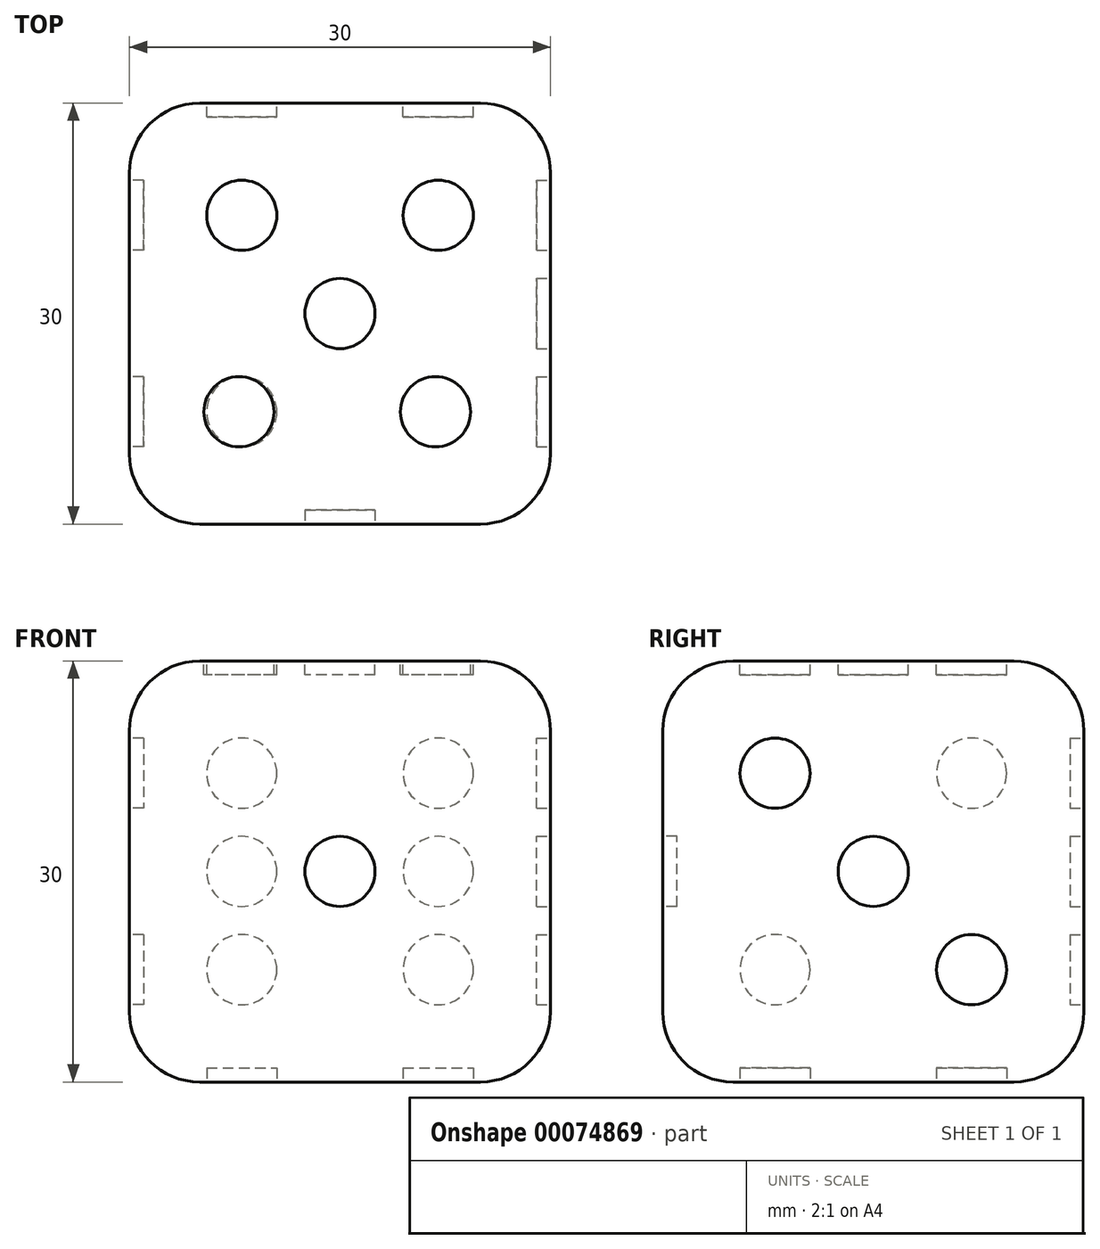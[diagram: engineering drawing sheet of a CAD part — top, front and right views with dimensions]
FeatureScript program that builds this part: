
annotation { "Feature Type Name" : "Feature", "Feature Type Description" : "" }
export const myFeature = defineFeature(function(context is Context, id is Id, definition is map)
    precondition{}
    {
        {
            var Q0;
            Q0=qCreatedBy(makeId("Front.planeOp"),FACE);
            var sketch = newSketch(context, id + "F0", { "sketchPlane" : qUnion([Q0])});
            skLineSegment(sketch, "E0.rect.bottom", {"start": v(-15, 15) * mm, "end": v(15, 15) * mm});
            skLineSegment(sketch, "E0.rect.top", {"start": v(-15, -15) * mm, "end": v(15, -15) * mm});
            skLineSegment(sketch, "E0.rect.left", {"start": v(-15, 15) * mm, "end": v(-15, -15) * mm});
            skLineSegment(sketch, "E0.rect.right", {"start": v(15, 15) * mm, "end": v(15, -15) * mm});
            skPoint(sketch, "E0.rect.middle", {"position": v(0, 0) * mm});
            skSolve(sketch);
        }
        {
            var Q0;
            Q0=makeQuery(id+"F0.imprint","IMPRINT",FACE,{"disambiguationData":[TD([[makeQuery(id+"F0.imprint","IMPRINT",EDGE,{"derivedFrom":sQuery(id+"F0.wireOp",EDGE,"E0.rect.bottom")}),-1.0]])]});
            extrude(context, id + "F1", {"entities" : qUnion([Q0]), "endBound" : BoundingType.SYMMETRIC, "depth" : 30 * mm});
        }
        {
            var Q0;
            Q0=makeQuery(id+"F1.opExtrude","CAP_FACE",FACE,{"disambiguationData":[OSD([sQuery(id+"F0.wireOp",EDGE,"E0.rect.bottom"),sQuery(id+"F0.wireOp",EDGE,"E0.rect.top"),sQuery(id+"F0.wireOp",EDGE,"E0.rect.left"),sQuery(id+"F0.wireOp",EDGE,"E0.rect.right")])],"isStart":false});
            var sketch = newSketch(context, id + "F2", { "sketchPlane" : qUnion([Q0])});
            skCircle(sketch, "E1", {"center": v(0, 0) * mm, "radius": 2.5 * mm});
            skSolve(sketch);
        }
        {
            var Q0;
            Q0=makeQuery(id+"F2.imprint","IMPRINT",FACE,{"disambiguationData":[TD([[makeQuery(id+"F2.imprint","IMPRINT",EDGE,{"derivedFrom":sQuery(id+"F2.wireOp",EDGE,"E1")}),1.0]])]});
            extrude(context, id + "F3", {"entities" : qUnion([Q0]), "operationType" : NewBodyOperationType.REMOVE, "oppositeDirection" : true, "depth" : 1 * mm});
        }
        {
            var Q0;
            Q0=makeQuery(id+"F1.opExtrude","CAP_FACE",FACE,{"disambiguationData":[OSD([sQuery(id+"F0.wireOp",EDGE,"E0.rect.bottom"),sQuery(id+"F0.wireOp",EDGE,"E0.rect.top"),sQuery(id+"F0.wireOp",EDGE,"E0.rect.left"),sQuery(id+"F0.wireOp",EDGE,"E0.rect.right")])],"isStart":true});
            var sketch = newSketch(context, id + "F4", { "sketchPlane" : qUnion([Q0])});
            skCircle(sketch, "E2", {"center": v(-7, 7) * mm, "radius": 2.5 * mm});
            skCircle(sketch, "E3.0.1.0", {"center": v(-7, 0) * mm, "radius": 2.5 * mm});
            skCircle(sketch, "E3.0.2.0", {"center": v(-7, -7) * mm, "radius": 2.5 * mm});
            skCircle(sketch, "E3.1.0.0", {"center": v(7, 7) * mm, "radius": 2.5 * mm});
            skCircle(sketch, "E3.1.1.0", {"center": v(7, 0) * mm, "radius": 2.5 * mm});
            skCircle(sketch, "E3.1.2.0", {"center": v(7, -7) * mm, "radius": 2.5 * mm});
            skLineSegment(sketch, "E3.direction1", {"start": v(-7, 7) * mm, "end": v(7, 7) * mm, "construction": true});
            skLineSegment(sketch, "E3.direction2", {"start": v(-7, 7) * mm, "end": v(-7, 0) * mm, "construction": true});
            skSolve(sketch);
        }
        {
            var Q0;
            Q0=makeQuery(id+"F4.imprint","IMPRINT",FACE,{"disambiguationData":[TD([[makeQuery(id+"F4.imprint","IMPRINT",EDGE,{"derivedFrom":sQuery(id+"F4.wireOp",EDGE,"E2")}),1.0]])]});
            var Q1;
            Q1=makeQuery(id+"F4.imprint","IMPRINT",FACE,{"disambiguationData":[TD([[makeQuery(id+"F4.imprint","IMPRINT",EDGE,{"derivedFrom":sQuery(id+"F4.wireOp",EDGE,"E3.0.1.0")}),1.0]])]});
            var Q2;
            Q2=makeQuery(id+"F4.imprint","IMPRINT",FACE,{"disambiguationData":[TD([[makeQuery(id+"F4.imprint","IMPRINT",EDGE,{"derivedFrom":sQuery(id+"F4.wireOp",EDGE,"E3.0.2.0")}),1.0]])]});
            var Q3;
            Q3=makeQuery(id+"F4.imprint","IMPRINT",FACE,{"disambiguationData":[TD([[makeQuery(id+"F4.imprint","IMPRINT",EDGE,{"derivedFrom":sQuery(id+"F4.wireOp",EDGE,"E3.1.2.0")}),1.0]])]});
            var Q4;
            Q4=makeQuery(id+"F4.imprint","IMPRINT",FACE,{"disambiguationData":[TD([[makeQuery(id+"F4.imprint","IMPRINT",EDGE,{"derivedFrom":sQuery(id+"F4.wireOp",EDGE,"E3.1.1.0")}),1.0]])]});
            var Q5;
            Q5=makeQuery(id+"F4.imprint","IMPRINT",FACE,{"disambiguationData":[TD([[makeQuery(id+"F4.imprint","IMPRINT",EDGE,{"derivedFrom":sQuery(id+"F4.wireOp",EDGE,"E3.1.0.0")}),1.0]])]});
            extrude(context, id + "F5", {"entities" : qUnion([Q0, Q1, Q2, Q3, Q4, Q5]), "operationType" : NewBodyOperationType.REMOVE, "oppositeDirection" : true, "depth" : 1 * mm});
        }
        {
            var Q0;
            Q0=makeQuery(id+"F1.opExtrude","SWEPT_FACE",FACE,{"disambiguationData":[OSD([sQuery(id+"F0.wireOp",EDGE,"E0.rect.right")])]});
            var sketch = newSketch(context, id + "F6", { "sketchPlane" : qUnion([Q0])});
            skCircle(sketch, "E4", {"center": v(0, 0) * mm, "radius": 2.5 * mm});
            skCircle(sketch, "E5", {"center": v(-7, 7) * mm, "radius": 2.5 * mm});
            skCircle(sketch, "E6", {"center": v(7, -7) * mm, "radius": 2.5 * mm});
            skSolve(sketch);
        }
        {
            var Q0;
            Q0=makeQuery(id+"F6.imprint","IMPRINT",FACE,{"disambiguationData":[TD([[makeQuery(id+"F6.imprint","IMPRINT",EDGE,{"derivedFrom":sQuery(id+"F6.wireOp",EDGE,"E5")}),1.0]])]});
            var Q1;
            Q1=makeQuery(id+"F6.imprint","IMPRINT",FACE,{"disambiguationData":[TD([[makeQuery(id+"F6.imprint","IMPRINT",EDGE,{"derivedFrom":sQuery(id+"F6.wireOp",EDGE,"E4")}),1.0]])]});
            var Q2;
            Q2=makeQuery(id+"F6.imprint","IMPRINT",FACE,{"disambiguationData":[TD([[makeQuery(id+"F6.imprint","IMPRINT",EDGE,{"derivedFrom":sQuery(id+"F6.wireOp",EDGE,"E6")}),1.0]])]});
            extrude(context, id + "F7", {"entities" : qUnion([Q0, Q1, Q2]), "operationType" : NewBodyOperationType.REMOVE, "oppositeDirection" : true, "depth" : 1 * mm});
        }
        {
            var Q0;
            Q0=makeQuery(id+"F1.opExtrude","SWEPT_FACE",FACE,{"disambiguationData":[OSD([sQuery(id+"F0.wireOp",EDGE,"E0.rect.left")])]});
            var sketch = newSketch(context, id + "F8", { "sketchPlane" : qUnion([Q0])});
            skCircle(sketch, "E7", {"center": v(-7, 7) * mm, "radius": 2.5 * mm});
            skCircle(sketch, "E8.0.1.0", {"center": v(-7, -7) * mm, "radius": 2.5 * mm});
            skCircle(sketch, "E8.1.0.0", {"center": v(7, 7) * mm, "radius": 2.5 * mm});
            skCircle(sketch, "E8.1.1.0", {"center": v(7, -7) * mm, "radius": 2.5 * mm});
            skLineSegment(sketch, "E8.direction1", {"start": v(-7, 7) * mm, "end": v(7, 7) * mm, "construction": true});
            skLineSegment(sketch, "E8.direction2", {"start": v(-7, 7) * mm, "end": v(-7, -7) * mm, "construction": true});
            skSolve(sketch);
        }
        {
            var Q0;
            Q0=makeQuery(id+"F8.imprint","IMPRINT",FACE,{"disambiguationData":[TD([[makeQuery(id+"F8.imprint","IMPRINT",EDGE,{"derivedFrom":sQuery(id+"F8.wireOp",EDGE,"E7")}),1.0]])]});
            var Q1;
            Q1=makeQuery(id+"F8.imprint","IMPRINT",FACE,{"disambiguationData":[TD([[makeQuery(id+"F8.imprint","IMPRINT",EDGE,{"derivedFrom":sQuery(id+"F8.wireOp",EDGE,"E8.1.0.0")}),1.0]])]});
            var Q2;
            Q2=makeQuery(id+"F8.imprint","IMPRINT",FACE,{"disambiguationData":[TD([[makeQuery(id+"F8.imprint","IMPRINT",EDGE,{"derivedFrom":sQuery(id+"F8.wireOp",EDGE,"E8.1.1.0")}),1.0]])]});
            var Q3;
            Q3=makeQuery(id+"F8.imprint","IMPRINT",FACE,{"disambiguationData":[TD([[makeQuery(id+"F8.imprint","IMPRINT",EDGE,{"derivedFrom":sQuery(id+"F8.wireOp",EDGE,"E8.0.1.0")}),1.0]])]});
            extrude(context, id + "F9", {"entities" : qUnion([Q0, Q1, Q2, Q3]), "operationType" : NewBodyOperationType.REMOVE, "oppositeDirection" : true, "depth" : 1 * mm});
        }
        {
            var Q0;
            Q0=makeQuery(id+"F1.opExtrude","SWEPT_FACE",FACE,{"disambiguationData":[OSD([sQuery(id+"F0.wireOp",EDGE,"E0.rect.bottom")])]});
            var sketch = newSketch(context, id + "F10", { "sketchPlane" : qUnion([Q0])});
            skCircle(sketch, "E9", {"center": v(0, 0) * mm, "radius": 2.5 * mm});
            skCircle(sketch, "E10", {"center": v(-7, 7) * mm, "radius": 2.5 * mm});
            skCircle(sketch, "E11.0.1.0", {"center": v(-7.2, -7) * mm, "radius": 2.5 * mm});
            skCircle(sketch, "E11.1.0.0", {"center": v(7, 7) * mm, "radius": 2.5 * mm});
            skCircle(sketch, "E11.1.1.0", {"center": v(6.8, -7) * mm, "radius": 2.5 * mm});
            skLineSegment(sketch, "E11.direction1", {"start": v(-7, 7) * mm, "end": v(7, 7) * mm, "construction": true});
            skLineSegment(sketch, "E11.direction2", {"start": v(-7, 7) * mm, "end": v(-7.2, -7) * mm, "construction": true});
            skSolve(sketch);
        }
        {
            var Q0;
            Q0=makeQuery(id+"F10.imprint","IMPRINT",FACE,{"disambiguationData":[TD([[makeQuery(id+"F10.imprint","IMPRINT",EDGE,{"derivedFrom":sQuery(id+"F10.wireOp",EDGE,"E11.1.1.0")}),1.0]])]});
            var Q1;
            Q1=makeQuery(id+"F10.imprint","IMPRINT",FACE,{"disambiguationData":[TD([[makeQuery(id+"F10.imprint","IMPRINT",EDGE,{"derivedFrom":sQuery(id+"F10.wireOp",EDGE,"E11.0.1.0")}),1.0]])]});
            var Q2;
            Q2=makeQuery(id+"F10.imprint","IMPRINT",FACE,{"disambiguationData":[TD([[makeQuery(id+"F10.imprint","IMPRINT",EDGE,{"derivedFrom":sQuery(id+"F10.wireOp",EDGE,"E9")}),1.0]])]});
            var Q3;
            Q3=makeQuery(id+"F10.imprint","IMPRINT",FACE,{"disambiguationData":[TD([[makeQuery(id+"F10.imprint","IMPRINT",EDGE,{"derivedFrom":sQuery(id+"F10.wireOp",EDGE,"E11.1.0.0")}),1.0]])]});
            var Q4;
            Q4=makeQuery(id+"F10.imprint","IMPRINT",FACE,{"disambiguationData":[TD([[makeQuery(id+"F10.imprint","IMPRINT",EDGE,{"derivedFrom":sQuery(id+"F10.wireOp",EDGE,"E10")}),1.0]])]});
            extrude(context, id + "F11", {"entities" : qUnion([Q0, Q1, Q2, Q3, Q4]), "operationType" : NewBodyOperationType.REMOVE, "oppositeDirection" : true, "depth" : 1 * mm});
        }
        {
            var Q0;
            Q0=makeQuery(id+"F1.opExtrude","SWEPT_FACE",FACE,{"disambiguationData":[OSD([sQuery(id+"F0.wireOp",EDGE,"E0.rect.top")])]});
            var sketch = newSketch(context, id + "F12", { "sketchPlane" : qUnion([Q0])});
            skCircle(sketch, "E12", {"center": v(-7, 7) * mm, "radius": 2.5 * mm});
            skCircle(sketch, "E13", {"center": v(7, -7) * mm, "radius": 2.5 * mm});
            skSolve(sketch);
        }
        {
            var Q0;
            Q0=makeQuery(id+"F12.imprint","IMPRINT",FACE,{"disambiguationData":[TD([[makeQuery(id+"F12.imprint","IMPRINT",EDGE,{"derivedFrom":sQuery(id+"F12.wireOp",EDGE,"E12")}),1.0]])]});
            var Q1;
            Q1=makeQuery(id+"F12.imprint","IMPRINT",FACE,{"disambiguationData":[TD([[makeQuery(id+"F12.imprint","IMPRINT",EDGE,{"derivedFrom":sQuery(id+"F12.wireOp",EDGE,"E13")}),1.0]])]});
            extrude(context, id + "F13", {"entities" : qUnion([Q0, Q1]), "operationType" : NewBodyOperationType.REMOVE, "oppositeDirection" : true, "depth" : 1 * mm});
        }
        {
            var Q0;
            Q0=makeQuery(id+"F1.opExtrude","SWEPT_EDGE",EDGE,{"disambiguationData":[OSD([sQuery(id+"F0.wireOp",EDGE,"E0.rect.bottom"),sQuery(id+"F0.wireOp",EDGE,"E0.rect.left")])]});
            var Q1;
            Q1=makeQuery(id+"F1.opExtrude","CAP_EDGE",EDGE,{"disambiguationData":[OSD([sQuery(id+"F0.wireOp",EDGE,"E0.rect.left")])],"isStart":true});
            var Q2;
            Q2=makeQuery(id+"F1.opExtrude","CAP_EDGE",EDGE,{"disambiguationData":[OSD([sQuery(id+"F0.wireOp",EDGE,"E0.rect.left")])],"isStart":false});
            var Q3;
            Q3=makeQuery(id+"F1.opExtrude","SWEPT_EDGE",EDGE,{"disambiguationData":[OSD([sQuery(id+"F0.wireOp",EDGE,"E0.rect.top"),sQuery(id+"F0.wireOp",EDGE,"E0.rect.left")])]});
            var Q4;
            Q4=makeQuery(id+"F1.opExtrude","CAP_EDGE",EDGE,{"disambiguationData":[OSD([sQuery(id+"F0.wireOp",EDGE,"E0.rect.top")])],"isStart":false});
            var Q5;
            Q5=makeQuery(id+"F1.opExtrude","CAP_EDGE",EDGE,{"disambiguationData":[OSD([sQuery(id+"F0.wireOp",EDGE,"E0.rect.bottom")])],"isStart":false});
            var Q6;
            Q6=makeQuery(id+"F1.opExtrude","CAP_EDGE",EDGE,{"disambiguationData":[OSD([sQuery(id+"F0.wireOp",EDGE,"E0.rect.right")])],"isStart":false});
            var Q7;
            Q7=makeQuery(id+"F1.opExtrude","CAP_EDGE",EDGE,{"disambiguationData":[OSD([sQuery(id+"F0.wireOp",EDGE,"E0.rect.top")])],"isStart":true});
            var Q8;
            Q8=makeQuery(id+"F1.opExtrude","SWEPT_EDGE",EDGE,{"disambiguationData":[OSD([sQuery(id+"F0.wireOp",EDGE,"E0.rect.top"),sQuery(id+"F0.wireOp",EDGE,"E0.rect.right")])]});
            var Q9;
            Q9=makeQuery(id+"F1.opExtrude","CAP_EDGE",EDGE,{"disambiguationData":[OSD([sQuery(id+"F0.wireOp",EDGE,"E0.rect.bottom")])],"isStart":true});
            var Q10;
            Q10=makeQuery(id+"F1.opExtrude","SWEPT_EDGE",EDGE,{"disambiguationData":[OSD([sQuery(id+"F0.wireOp",EDGE,"E0.rect.bottom"),sQuery(id+"F0.wireOp",EDGE,"E0.rect.right")])]});
            var Q11;
            Q11=makeQuery(id+"F1.opExtrude","CAP_EDGE",EDGE,{"disambiguationData":[OSD([sQuery(id+"F0.wireOp",EDGE,"E0.rect.right")])],"isStart":true});
            fillet(context, id + "F14", {"entities" : qUnion([Q0, Q1, Q2, Q3, Q4, Q5, Q6, Q7, Q8, Q9, Q10, Q11]), "radius" : 5 * mm, "tangentPropagation" : true, "allowEdgeOverflow" : false});
        }
    });
